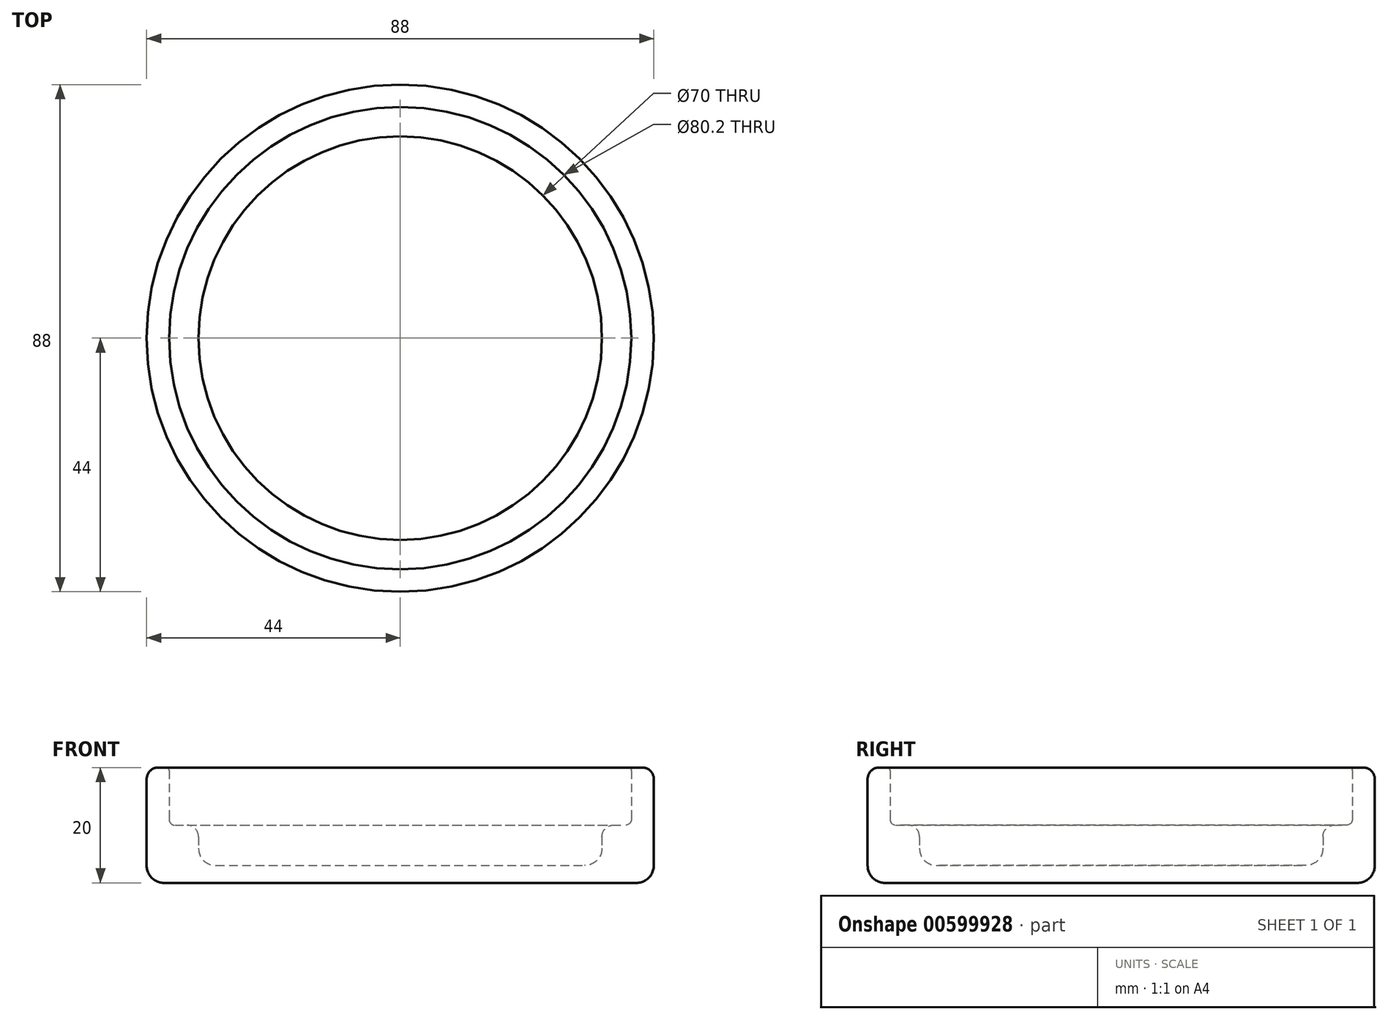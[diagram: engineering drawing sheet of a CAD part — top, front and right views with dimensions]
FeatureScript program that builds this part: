
annotation { "Feature Type Name" : "Feature", "Feature Type Description" : "" }
export const myFeature = defineFeature(function(context is Context, id is Id, definition is map)
    precondition{}
    {
        {
            var Q0;
            Q0=qCreatedBy(makeId("Front.planeOp"),FACE);
            var sketch = newSketch(context, id + "F0", { "sketchPlane" : qUnion([Q0])});
            skLineSegment(sketch, "E0", {"start": v(0, 0) * mm, "end": v(-35, 0) * mm});
            skLineSegment(sketch, "E1", {"start": v(-35, 0) * mm, "end": v(-35, 7) * mm});
            skLineSegment(sketch, "E2", {"start": v(-35, 7) * mm, "end": v(-40.1, 7) * mm});
            skLineSegment(sketch, "E3", {"start": v(-40.1, 7) * mm, "end": v(-40.1, 17) * mm});
            skLineSegment(sketch, "E4", {"start": v(-40.1, 17) * mm, "end": v(-44, 17) * mm});
            skLineSegment(sketch, "E5", {"start": v(-44, 17) * mm, "end": v(-44, 0) * mm});
            skLineSegment(sketch, "E6", {"start": v(-41, -3) * mm, "end": v(0, -3) * mm});
            skLineSegment(sketch, "E7", {"start": v(0, -3) * mm, "end": v(0, 0) * mm});
            skPoint(sketch, "E8.visualSharp", {"position": v(-44, -3) * mm});
            skArc(sketch, "E8.filletArc", {"start": v(-44, 0) * mm, "mid": v(-43.12, -2.12) * mm, "end": v(-41, -3) * mm});
            skSolve(sketch);
        }
        {
            var Q0;
            Q0=makeQuery(id+"F0.imprint","IMPRINT",FACE,{"disambiguationData":[TD([[makeQuery(id+"F0.imprint","IMPRINT",EDGE,{"derivedFrom":sQuery(id+"F0.wireOp",EDGE,"E0")}),1.0]])]});
            var Q1;
            Q1=sQuery(id+"F0.wireOp",EDGE,"E7");
            revolve(context, id + "F1", {"entities" : qUnion([Q0]), "axis" : qUnion([Q1]), "revolveType" : RevolveType.FULL});
        }
        {
            var Q0;
            Q0=makeQuery(id+"F1.opRevolve","SWEPT_FACE",FACE,{"disambiguationData":[OSD([sQuery(id+"F0.wireOp",EDGE,"E0")])]});
            fillet(context, id + "F2", {"entities" : qUnion([Q0]), "radius" : 3 * mm, "tangentPropagation" : true, "allowEdgeOverflow" : false});
        }
        {
            var Q0;
            Q0=makeQuery(id+"F1.opRevolve","SWEPT_EDGE",EDGE,{"disambiguationData":[OSD([sQuery(id+"F0.wireOp",EDGE,"E1"),sQuery(id+"F0.wireOp",EDGE,"E2")])]});
            fillet(context, id + "F3", {"entities" : qUnion([Q0]), "radius" : 2 * mm, "tangentPropagation" : true, "allowEdgeOverflow" : false});
        }
        {
            var Q0;
            Q0=makeQuery(id+"F1.opRevolve","SWEPT_EDGE",EDGE,{"disambiguationData":[OSD([sQuery(id+"F0.wireOp",EDGE,"E4"),sQuery(id+"F0.wireOp",EDGE,"E5")])]});
            fillet(context, id + "F4", {"entities" : qUnion([Q0]), "radius" : 2 * mm, "tangentPropagation" : true, "allowEdgeOverflow" : false});
        }
        {
            var Q0;
            Q0=makeQuery(id+"F1.opRevolve","SWEPT_EDGE",EDGE,{"disambiguationData":[OSD([sQuery(id+"F0.wireOp",EDGE,"E3"),sQuery(id+"F0.wireOp",EDGE,"E4")])]});
            fillet(context, id + "F5", {"entities" : qUnion([Q0]), "radius" : 0.5 * mm, "tangentPropagation" : true, "allowEdgeOverflow" : false});
        }
        {
            var Q0;
            Q0=makeQuery(id+"F1.opRevolve","SWEPT_EDGE",EDGE,{"disambiguationData":[OSD([sQuery(id+"F0.wireOp",EDGE,"E2"),sQuery(id+"F0.wireOp",EDGE,"E3")])]});
            fillet(context, id + "F6", {"entities" : qUnion([Q0]), "radius" : 1 * mm, "tangentPropagation" : true, "allowEdgeOverflow" : false});
        }
    });
